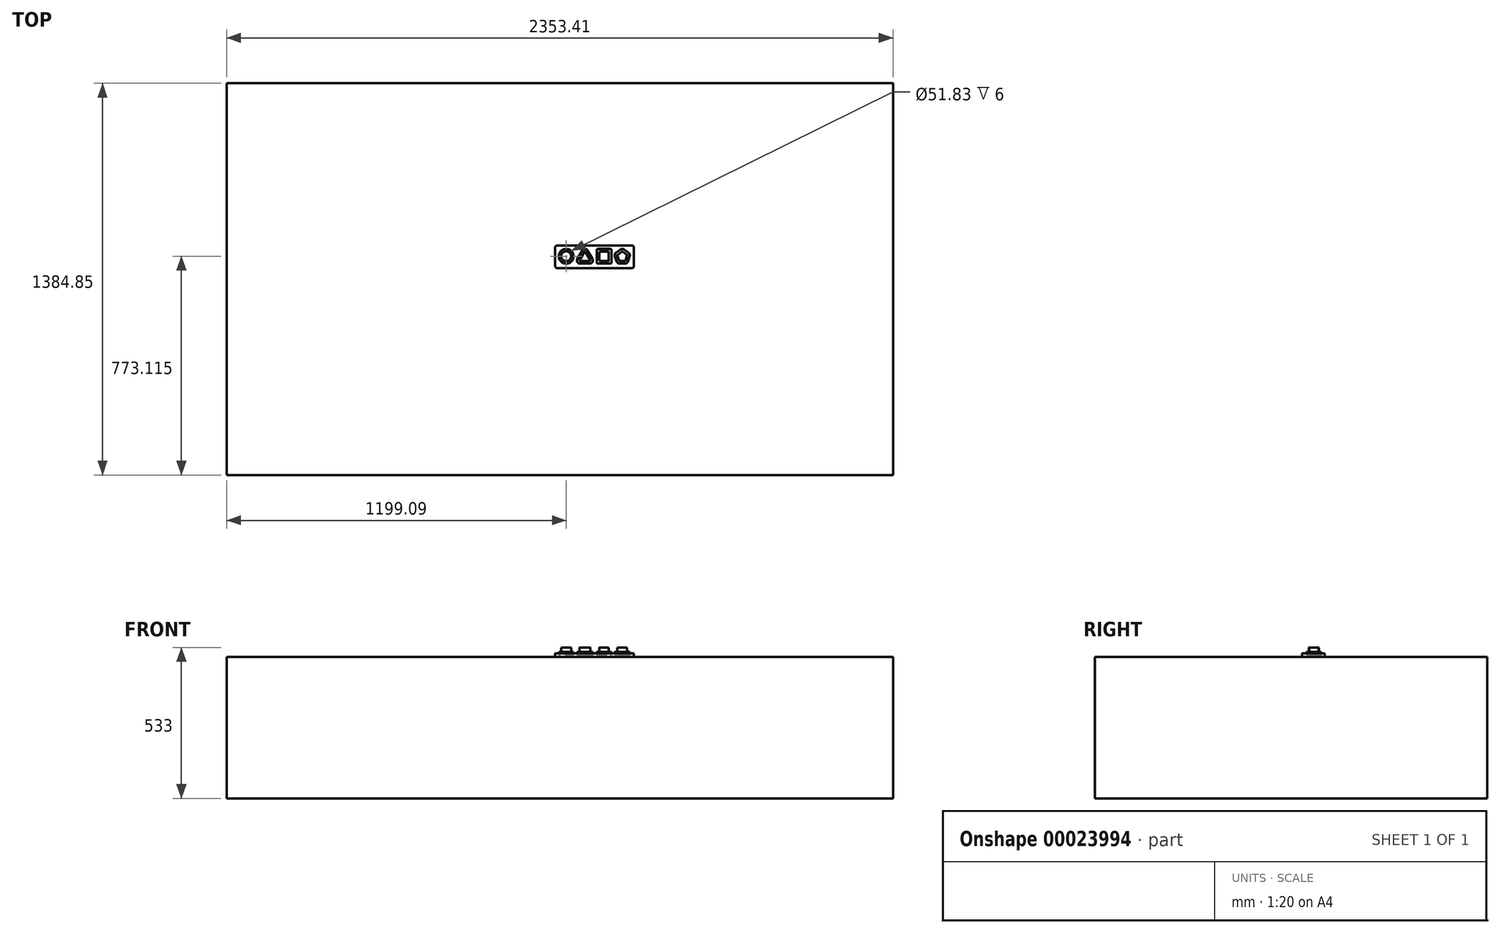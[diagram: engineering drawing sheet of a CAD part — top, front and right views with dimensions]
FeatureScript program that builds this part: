
annotation { "Feature Type Name" : "Feature", "Feature Type Description" : "" }
export const myFeature = defineFeature(function(context is Context, id is Id, definition is map)
    precondition{}
    {
        {
            var Q0;
            Q0=qCreatedBy(makeId("Top.planeOp"),FACE);
            var sketch = newSketch(context, id + "F0", { "sketchPlane" : qUnion([Q0])});
            skLineSegment(sketch, "E0.bottom", {"start": v(-140, 12) * mm, "end": v(124, 12) * mm});
            skLineSegment(sketch, "E0.top", {"start": v(-140, -68) * mm, "end": v(124, -68) * mm});
            skLineSegment(sketch, "E0.left", {"start": v(-147, 5) * mm, "end": v(-147, -61) * mm});
            skLineSegment(sketch, "E0.right", {"start": v(131, 5) * mm, "end": v(131, -61) * mm});
            skLineSegment(sketch, "E1.bottom", {"start": v(5, 0) * mm, "end": v(47, 0) * mm});
            skLineSegment(sketch, "E1.top", {"start": v(5, -52) * mm, "end": v(47, -52) * mm});
            skLineSegment(sketch, "E1.left", {"start": v(0, -5) * mm, "end": v(0, -47) * mm});
            skLineSegment(sketch, "E1.right", {"start": v(52, -5) * mm, "end": v(52, -47) * mm});
            skCircle(sketch, "E2", {"center": v(-108.08, -26.08) * mm, "radius": 25.92 * mm});
            skLineSegment(sketch, "E3", {"start": v(0, 120.87) * mm, "end": v(0, -115.92) * mm, "construction": true});
            skPoint(sketch, "E4.visualSharp", {"position": v(0, -52) * mm});
            skArc(sketch, "E4.filletArc", {"start": v(0, -47) * mm, "mid": v(1.46, -50.54) * mm, "end": v(5, -52) * mm});
            skPoint(sketch, "E5.visualSharp", {"position": v(0, 0) * mm});
            skArc(sketch, "E5.filletArc", {"start": v(5, 0) * mm, "mid": v(1.46, -1.46) * mm, "end": v(0, -5) * mm});
            skPoint(sketch, "E6.visualSharp", {"position": v(52, 0) * mm});
            skArc(sketch, "E6.filletArc", {"start": v(52, -5) * mm, "mid": v(50.54, -1.46) * mm, "end": v(47, 0) * mm});
            skPoint(sketch, "E7.visualSharp", {"position": v(52, -52) * mm});
            skArc(sketch, "E7.filletArc", {"start": v(47, -52) * mm, "mid": v(50.54, -50.54) * mm, "end": v(52, -47) * mm});
            skPoint(sketch, "E8.visualSharp", {"position": v(-1.47, -51.53) * mm});
            skPoint(sketch, "E9.visualSharp", {"position": v(-147, 12) * mm});
            skArc(sketch, "E9.filletArc", {"start": v(-140, 12) * mm, "mid": v(-144.95, 9.95) * mm, "end": v(-147, 5) * mm});
            skPoint(sketch, "E10.visualSharp", {"position": v(131, 12) * mm});
            skArc(sketch, "E10.filletArc", {"start": v(131, 5) * mm, "mid": v(128.95, 9.95) * mm, "end": v(124, 12) * mm});
            skPoint(sketch, "E11.visualSharp", {"position": v(131, -68) * mm});
            skArc(sketch, "E11.filletArc", {"start": v(124, -68) * mm, "mid": v(128.95, -65.95) * mm, "end": v(131, -61) * mm});
            skPoint(sketch, "E12.visualSharp", {"position": v(-147, -68) * mm});
            skArc(sketch, "E12.filletArc", {"start": v(-147, -61) * mm, "mid": v(-144.95, -65.95) * mm, "end": v(-140, -68) * mm});
            skLineSegment(sketch, "E13", {"start": v(-178.87, 0) * mm, "end": v(142.51, 0) * mm, "construction": true});
            skLineSegment(sketch, "E14", {"start": v(-177.03, -52) * mm, "end": v(135.64, -52) * mm, "construction": true});
            skCircle(sketch, "E15.cCircle", {"center": v(-42, -30.98) * mm, "radius": 42.04 * mm, "construction": true});
            skLineSegment(sketch, "E15.0", {"start": v(-32.47, -5.45) * mm, "end": v(-15.12, -35.5) * mm});
            skLineSegment(sketch, "E15.1", {"start": v(-24.65, -52) * mm, "end": v(-59.35, -52) * mm});
            skLineSegment(sketch, "E15.2", {"start": v(-68.88, -35.5) * mm, "end": v(-51.53, -5.45) * mm});
            skCircle(sketch, "E16.cCircle", {"center": v(90, -27.6) * mm, "radius": 30.15 * mm, "construction": true});
            skLineSegment(sketch, "E16.0", {"start": v(96.47, -2.16) * mm, "end": v(112.2, -13.6) * mm});
            skLineSegment(sketch, "E16.1", {"start": v(116.2, -25.9) * mm, "end": v(110.2, -44.4) * mm});
            skLineSegment(sketch, "E16.2", {"start": v(99.73, -52) * mm, "end": v(80.27, -52) * mm});
            skLineSegment(sketch, "E16.3", {"start": v(69.8, -44.4) * mm, "end": v(63.8, -25.9) * mm});
            skLineSegment(sketch, "E16.4", {"start": v(67.8, -13.6) * mm, "end": v(83.53, -2.16) * mm});
            skPoint(sketch, "E17.visualSharp", {"position": v(-78.4, -52) * mm});
            skArc(sketch, "E17.filletArc", {"start": v(-68.88, -35.5) * mm, "mid": v(-68.88, -46.5) * mm, "end": v(-59.35, -52) * mm});
            skPoint(sketch, "E18.visualSharp", {"position": v(-42, 11.05) * mm});
            skArc(sketch, "E18.filletArc", {"start": v(-32.47, -5.45) * mm, "mid": v(-42, 0.05) * mm, "end": v(-51.53, -5.45) * mm});
            skPoint(sketch, "E19.visualSharp", {"position": v(-5.6, -52) * mm});
            skArc(sketch, "E19.filletArc", {"start": v(-24.65, -52) * mm, "mid": v(-15.12, -46.5) * mm, "end": v(-15.12, -35.5) * mm});
            skPoint(sketch, "E20.visualSharp", {"position": v(61.33, -18.3) * mm});
            skArc(sketch, "E20.filletArc", {"start": v(67.8, -13.6) * mm, "mid": v(63.8, -19.1) * mm, "end": v(63.8, -25.9) * mm});
            skPoint(sketch, "E21.visualSharp", {"position": v(90, 2.54) * mm});
            skArc(sketch, "E21.filletArc", {"start": v(96.47, -2.16) * mm, "mid": v(90, -0.06) * mm, "end": v(83.53, -2.16) * mm});
            skPoint(sketch, "E22.visualSharp", {"position": v(118.67, -18.3) * mm});
            skArc(sketch, "E22.filletArc", {"start": v(116.2, -25.9) * mm, "mid": v(116.2, -19.1) * mm, "end": v(112.2, -13.6) * mm});
            skPoint(sketch, "E23.visualSharp", {"position": v(107.72, -52) * mm});
            skArc(sketch, "E23.filletArc", {"start": v(99.73, -52) * mm, "mid": v(106.2, -49.9) * mm, "end": v(110.2, -44.4) * mm});
            skPoint(sketch, "E24.visualSharp", {"position": v(72.28, -52) * mm});
            skArc(sketch, "E24.filletArc", {"start": v(69.8, -44.4) * mm, "mid": v(73.8, -49.9) * mm, "end": v(80.27, -52) * mm});
            skSolve(sketch);
        }
        {
            var Q0;
            Q0 = qSketchRegion(id + "F0", true);
            extrude(context, id + "F1", {"entities" : qUnion([Q0]), "depth" : 6 * mm});
        }
        {
            var Q0;
            Q0=makeQuery(id+"F1.opExtrude","CAP_FACE",FACE,{"disambiguationData":[OSD([sQuery(id+"F0.wireOp",EDGE,"E0.bottom"),sQuery(id+"F0.wireOp",EDGE,"E0.top"),sQuery(id+"F0.wireOp",EDGE,"E0.left"),sQuery(id+"F0.wireOp",EDGE,"E0.right"),sQuery(id+"F0.wireOp",EDGE,"E1.bottom"),sQuery(id+"F0.wireOp",EDGE,"E1.top"),sQuery(id+"F0.wireOp",EDGE,"E1.left"),sQuery(id+"F0.wireOp",EDGE,"E1.right"),sQuery(id+"F0.wireOp",EDGE,"E2"),sQuery(id+"F0.wireOp",EDGE,"869f132f-bd3b-4005-ba41-de87afd1fafc.0"),sQuery(id+"F0.wireOp",EDGE,"869f132f-bd3b-4005-ba41-de87afd1fafc.1"),sQuery(id+"F0.wireOp",EDGE,"869f132f-bd3b-4005-ba41-de87afd1fafc.2"),sQuery(id+"F0.wireOp",EDGE,"28d936d4-a283-45c8-93be-50b37cede906.0"),sQuery(id+"F0.wireOp",EDGE,"28d936d4-a283-45c8-93be-50b37cede906.1"),sQuery(id+"F0.wireOp",EDGE,"28d936d4-a283-45c8-93be-50b37cede906.2"),sQuery(id+"F0.wireOp",EDGE,"28d936d4-a283-45c8-93be-50b37cede906.3"),sQuery(id+"F0.wireOp",EDGE,"28d936d4-a283-45c8-93be-50b37cede906.4"),sQuery(id+"F0.wireOp",EDGE,"E4.filletArc"),sQuery(id+"F0.wireOp",EDGE,"E5.filletArc"),sQuery(id+"F0.wireOp",EDGE,"E6.filletArc"),sQuery(id+"F0.wireOp",EDGE,"E7.filletArc"),sQuery(id+"F0.wireOp",EDGE,"e9b6b36f-3266-419f-b830-8cc76e1a5d8f.filletArc"),sQuery(id+"F0.wireOp",EDGE,"cbe3ce96-ce12-412b-8ec9-2c38098c0a51.filletArc"),sQuery(id+"F0.wireOp",EDGE,"E8.filletArc"),sQuery(id+"F0.wireOp",EDGE,"ebdce603-2f92-4f1c-9763-50f2206a4805.filletArc"),sQuery(id+"F0.wireOp",EDGE,"32bf3db0-3fe5-4774-a2ea-bb73315c0dd0.filletArc"),sQuery(id+"F0.wireOp",EDGE,"89093162-53c0-41e8-8220-2e7c1048e818.filletArc"),sQuery(id+"F0.wireOp",EDGE,"d950af28-5088-4348-9f62-8025f05ed35f.filletArc"),sQuery(id+"F0.wireOp",EDGE,"a5eb8416-0ce1-40eb-8187-346b929c9b26.filletArc"),sQuery(id+"F0.wireOp",EDGE,"E9.filletArc"),sQuery(id+"F0.wireOp",EDGE,"E10.filletArc"),sQuery(id+"F0.wireOp",EDGE,"E11.filletArc"),sQuery(id+"F0.wireOp",EDGE,"E12.filletArc")])],"isStart":false});
            var sketch = newSketch(context, id + "F2", { "sketchPlane" : qUnion([Q0])});
            skCircle(sketch, "E25.0", {"center": v(-108.08, -26.08) * mm, "radius": 25.42 * mm});
            skSolve(sketch);
        }
        {
            var Q0;
            Q0 = qSketchRegion(id + "F2", true);
            extrude(context, id + "F3", {"entities" : qUnion([Q0]), "depth" : 6 * mm});
        }
        {
            var Q0;
            Q0=makeQuery(id+"F3.opExtrude","CAP_FACE",FACE,{"disambiguationData":[OSD([sQuery(id+"F2.wireOp",EDGE,"E25.0")])],"isStart":false});
            var sketch = newSketch(context, id + "F4", { "sketchPlane" : qUnion([Q0])});
            skCircle(sketch, "E26.0", {"center": v(-108.08, -26.08) * mm, "radius": 17.42 * mm});
            skSolve(sketch);
        }
        {
            var Q0;
            Q0 = qSketchRegion(id + "F4", true);
            extrude(context, id + "F5", {"entities" : qUnion([Q0]), "operationType" : NewBodyOperationType.ADD, "depth" : 15 * mm});
        }
        {
            var Q0;
            Q0=makeQuery(id+"F1.opExtrude","CAP_FACE",FACE,{"disambiguationData":[OSD([sQuery(id+"F0.wireOp",EDGE,"E0.bottom"),sQuery(id+"F0.wireOp",EDGE,"E0.top"),sQuery(id+"F0.wireOp",EDGE,"E0.left"),sQuery(id+"F0.wireOp",EDGE,"E0.right"),sQuery(id+"F0.wireOp",EDGE,"E1.bottom"),sQuery(id+"F0.wireOp",EDGE,"E1.top"),sQuery(id+"F0.wireOp",EDGE,"E1.left"),sQuery(id+"F0.wireOp",EDGE,"E1.right"),sQuery(id+"F0.wireOp",EDGE,"E2"),sQuery(id+"F0.wireOp",EDGE,"E4.filletArc"),sQuery(id+"F0.wireOp",EDGE,"E5.filletArc"),sQuery(id+"F0.wireOp",EDGE,"E6.filletArc"),sQuery(id+"F0.wireOp",EDGE,"E7.filletArc"),sQuery(id+"F0.wireOp",EDGE,"E9.filletArc"),sQuery(id+"F0.wireOp",EDGE,"E10.filletArc"),sQuery(id+"F0.wireOp",EDGE,"E11.filletArc"),sQuery(id+"F0.wireOp",EDGE,"E12.filletArc"),sQuery(id+"F0.wireOp",EDGE,"E15.0"),sQuery(id+"F0.wireOp",EDGE,"E15.1"),sQuery(id+"F0.wireOp",EDGE,"E15.2"),sQuery(id+"F0.wireOp",EDGE,"E16.0"),sQuery(id+"F0.wireOp",EDGE,"E16.1"),sQuery(id+"F0.wireOp",EDGE,"E16.2"),sQuery(id+"F0.wireOp",EDGE,"E16.3"),sQuery(id+"F0.wireOp",EDGE,"E16.4"),sQuery(id+"F0.wireOp",EDGE,"E17.filletArc"),sQuery(id+"F0.wireOp",EDGE,"E18.filletArc"),sQuery(id+"F0.wireOp",EDGE,"E19.filletArc"),sQuery(id+"F0.wireOp",EDGE,"E20.filletArc"),sQuery(id+"F0.wireOp",EDGE,"E21.filletArc"),sQuery(id+"F0.wireOp",EDGE,"E22.filletArc"),sQuery(id+"F0.wireOp",EDGE,"E23.filletArc"),sQuery(id+"F0.wireOp",EDGE,"E24.filletArc")])],"isStart":false});
            var sketch = newSketch(context, id + "F6", { "sketchPlane" : qUnion([Q0])});
            skLineSegment(sketch, "E27.0", {"start": v(-68.45, -35.75) * mm, "end": v(-51.1, -5.7) * mm});
            skArc(sketch, "E27.1", {"start": v(-68.45, -35.75) * mm, "mid": v(-68.45, -46.25) * mm, "end": v(-59.35, -51.5) * mm});
            skLineSegment(sketch, "E27.2", {"start": v(-24.65, -51.5) * mm, "end": v(-59.35, -51.5) * mm});
            skArc(sketch, "E27.3", {"start": v(-24.65, -51.5) * mm, "mid": v(-15.55, -46.25) * mm, "end": v(-15.55, -35.75) * mm});
            skLineSegment(sketch, "E27.4", {"start": v(-32.9, -5.7) * mm, "end": v(-15.55, -35.75) * mm});
            skArc(sketch, "E27.5", {"start": v(-32.9, -5.7) * mm, "mid": v(-42, -0.45) * mm, "end": v(-51.1, -5.7) * mm});
            skSolve(sketch);
        }
        {
            var Q0;
            Q0 = qSketchRegion(id + "F6", true);
            extrude(context, id + "F7", {"entities" : qUnion([Q0]), "depth" : 6 * mm});
        }
        {
            var Q0;
            Q0=makeQuery(id+"F7.opExtrude","CAP_FACE",FACE,{"disambiguationData":[OSD([sQuery(id+"F6.wireOp",EDGE,"E27.0"),sQuery(id+"F6.wireOp",EDGE,"E27.1"),sQuery(id+"F6.wireOp",EDGE,"E27.2"),sQuery(id+"F6.wireOp",EDGE,"E27.3"),sQuery(id+"F6.wireOp",EDGE,"E27.4"),sQuery(id+"F6.wireOp",EDGE,"E27.5")])],"isStart":false});
            var sketch = newSketch(context, id + "F8", { "sketchPlane" : qUnion([Q0])});
            skLineSegment(sketch, "E28.0", {"start": v(-60.65, -40.25) * mm, "end": v(-43.3, -10.2) * mm});
            skArc(sketch, "E28.1", {"start": v(-60.65, -40.25) * mm, "mid": v(-60.65, -41.75) * mm, "end": v(-59.35, -42.5) * mm});
            skLineSegment(sketch, "E28.2", {"start": v(-24.65, -42.5) * mm, "end": v(-59.35, -42.5) * mm});
            skArc(sketch, "E28.3", {"start": v(-24.65, -42.5) * mm, "mid": v(-23.35, -41.75) * mm, "end": v(-23.35, -40.25) * mm});
            skLineSegment(sketch, "E28.4", {"start": v(-40.7, -10.2) * mm, "end": v(-23.35, -40.25) * mm});
            skArc(sketch, "E28.5", {"start": v(-40.7, -10.2) * mm, "mid": v(-42, -9.45) * mm, "end": v(-43.3, -10.2) * mm});
            skSolve(sketch);
        }
        {
            var Q0;
            Q0 = qSketchRegion(id + "F8", true);
            extrude(context, id + "F9", {"entities" : qUnion([Q0]), "operationType" : NewBodyOperationType.ADD, "depth" : 15 * mm});
        }
        {
            var Q0;
            Q0=makeQuery(id+"F1.opExtrude","CAP_FACE",FACE,{"disambiguationData":[OSD([sQuery(id+"F0.wireOp",EDGE,"E0.bottom"),sQuery(id+"F0.wireOp",EDGE,"E0.top"),sQuery(id+"F0.wireOp",EDGE,"E0.left"),sQuery(id+"F0.wireOp",EDGE,"E0.right"),sQuery(id+"F0.wireOp",EDGE,"E1.bottom"),sQuery(id+"F0.wireOp",EDGE,"E1.top"),sQuery(id+"F0.wireOp",EDGE,"E1.left"),sQuery(id+"F0.wireOp",EDGE,"E1.right"),sQuery(id+"F0.wireOp",EDGE,"E2"),sQuery(id+"F0.wireOp",EDGE,"E4.filletArc"),sQuery(id+"F0.wireOp",EDGE,"E5.filletArc"),sQuery(id+"F0.wireOp",EDGE,"E6.filletArc"),sQuery(id+"F0.wireOp",EDGE,"E7.filletArc"),sQuery(id+"F0.wireOp",EDGE,"E9.filletArc"),sQuery(id+"F0.wireOp",EDGE,"E10.filletArc"),sQuery(id+"F0.wireOp",EDGE,"E11.filletArc"),sQuery(id+"F0.wireOp",EDGE,"E12.filletArc"),sQuery(id+"F0.wireOp",EDGE,"E15.0"),sQuery(id+"F0.wireOp",EDGE,"E15.1"),sQuery(id+"F0.wireOp",EDGE,"E15.2"),sQuery(id+"F0.wireOp",EDGE,"E16.0"),sQuery(id+"F0.wireOp",EDGE,"E16.1"),sQuery(id+"F0.wireOp",EDGE,"E16.2"),sQuery(id+"F0.wireOp",EDGE,"E16.3"),sQuery(id+"F0.wireOp",EDGE,"E16.4"),sQuery(id+"F0.wireOp",EDGE,"E17.filletArc"),sQuery(id+"F0.wireOp",EDGE,"E18.filletArc"),sQuery(id+"F0.wireOp",EDGE,"E19.filletArc"),sQuery(id+"F0.wireOp",EDGE,"E20.filletArc"),sQuery(id+"F0.wireOp",EDGE,"E21.filletArc"),sQuery(id+"F0.wireOp",EDGE,"E22.filletArc"),sQuery(id+"F0.wireOp",EDGE,"E23.filletArc"),sQuery(id+"F0.wireOp",EDGE,"E24.filletArc")])],"isStart":false});
            var sketch = newSketch(context, id + "F10", { "sketchPlane" : qUnion([Q0])});
            skArc(sketch, "E29.0", {"start": v(5, -0.5) * mm, "mid": v(1.82, -1.82) * mm, "end": v(0.5, -5) * mm});
            skLineSegment(sketch, "E29.1", {"start": v(0.5, -5) * mm, "end": v(0.5, -47) * mm});
            skArc(sketch, "E29.2", {"start": v(0.5, -47) * mm, "mid": v(1.82, -50.18) * mm, "end": v(5, -51.5) * mm});
            skLineSegment(sketch, "E29.3", {"start": v(5, -51.5) * mm, "end": v(47, -51.5) * mm});
            skArc(sketch, "E29.4", {"start": v(47, -51.5) * mm, "mid": v(50.18, -50.18) * mm, "end": v(51.5, -47) * mm});
            skLineSegment(sketch, "E29.5", {"start": v(5, -0.5) * mm, "end": v(47, -0.5) * mm});
            skLineSegment(sketch, "E29.6", {"start": v(51.5, -5) * mm, "end": v(51.5, -47) * mm});
            skArc(sketch, "E29.7", {"start": v(51.5, -5) * mm, "mid": v(50.18, -1.82) * mm, "end": v(47, -0.5) * mm});
            skSolve(sketch);
        }
        {
            var Q0;
            Q0 = qSketchRegion(id + "F10", true);
            extrude(context, id + "F11", {"entities" : qUnion([Q0]), "depth" : 6 * mm});
        }
        {
            var Q0;
            Q0=makeQuery(id+"F11.opExtrude","CAP_FACE",FACE,{"disambiguationData":[OSD([sQuery(id+"F10.wireOp",EDGE,"E29.0"),sQuery(id+"F10.wireOp",EDGE,"E29.1"),sQuery(id+"F10.wireOp",EDGE,"E29.2"),sQuery(id+"F10.wireOp",EDGE,"E29.3"),sQuery(id+"F10.wireOp",EDGE,"E29.4"),sQuery(id+"F10.wireOp",EDGE,"E29.5"),sQuery(id+"F10.wireOp",EDGE,"E29.6"),sQuery(id+"F10.wireOp",EDGE,"E29.7")])],"isStart":false});
            var sketch = newSketch(context, id + "F12", { "sketchPlane" : qUnion([Q0])});
            skLineSegment(sketch, "E30.0", {"start": v(11.5, -9.5) * mm, "end": v(40.5, -9.5) * mm});
            skLineSegment(sketch, "E30.1", {"start": v(9.5, -11.5) * mm, "end": v(9.5, -40.5) * mm});
            skLineSegment(sketch, "E30.2", {"start": v(11.5, -42.5) * mm, "end": v(40.5, -42.5) * mm});
            skLineSegment(sketch, "E30.3", {"start": v(42.5, -11.5) * mm, "end": v(42.5, -40.5) * mm});
            skPoint(sketch, "E31.visualSharp", {"position": v(9.5, -9.5) * mm});
            skArc(sketch, "E31.filletArc", {"start": v(11.5, -9.5) * mm, "mid": v(10.09, -10.09) * mm, "end": v(9.5, -11.5) * mm});
            skPoint(sketch, "E32.visualSharp", {"position": v(42.5, -9.5) * mm});
            skArc(sketch, "E32.filletArc", {"start": v(42.5, -11.5) * mm, "mid": v(41.91, -10.09) * mm, "end": v(40.5, -9.5) * mm});
            skPoint(sketch, "E33.visualSharp", {"position": v(42.5, -42.5) * mm});
            skArc(sketch, "E33.filletArc", {"start": v(40.5, -42.5) * mm, "mid": v(41.91, -41.91) * mm, "end": v(42.5, -40.5) * mm});
            skPoint(sketch, "E34.visualSharp", {"position": v(9.5, -42.5) * mm});
            skArc(sketch, "E34.filletArc", {"start": v(9.5, -40.5) * mm, "mid": v(10.09, -41.91) * mm, "end": v(11.5, -42.5) * mm});
            skSolve(sketch);
        }
        {
            var Q0;
            Q0 = qSketchRegion(id + "F12", true);
            extrude(context, id + "F13", {"entities" : qUnion([Q0]), "operationType" : NewBodyOperationType.ADD, "depth" : 15 * mm});
        }
        {
            var Q0;
            Q0=makeQuery(id+"F1.opExtrude","CAP_FACE",FACE,{"disambiguationData":[OSD([sQuery(id+"F0.wireOp",EDGE,"E0.bottom"),sQuery(id+"F0.wireOp",EDGE,"E0.top"),sQuery(id+"F0.wireOp",EDGE,"E0.left"),sQuery(id+"F0.wireOp",EDGE,"E0.right"),sQuery(id+"F0.wireOp",EDGE,"E1.bottom"),sQuery(id+"F0.wireOp",EDGE,"E1.top"),sQuery(id+"F0.wireOp",EDGE,"E1.left"),sQuery(id+"F0.wireOp",EDGE,"E1.right"),sQuery(id+"F0.wireOp",EDGE,"E2"),sQuery(id+"F0.wireOp",EDGE,"E4.filletArc"),sQuery(id+"F0.wireOp",EDGE,"E5.filletArc"),sQuery(id+"F0.wireOp",EDGE,"E6.filletArc"),sQuery(id+"F0.wireOp",EDGE,"E7.filletArc"),sQuery(id+"F0.wireOp",EDGE,"E9.filletArc"),sQuery(id+"F0.wireOp",EDGE,"E10.filletArc"),sQuery(id+"F0.wireOp",EDGE,"E11.filletArc"),sQuery(id+"F0.wireOp",EDGE,"E12.filletArc"),sQuery(id+"F0.wireOp",EDGE,"E15.0"),sQuery(id+"F0.wireOp",EDGE,"E15.1"),sQuery(id+"F0.wireOp",EDGE,"E15.2"),sQuery(id+"F0.wireOp",EDGE,"E16.0"),sQuery(id+"F0.wireOp",EDGE,"E16.1"),sQuery(id+"F0.wireOp",EDGE,"E16.2"),sQuery(id+"F0.wireOp",EDGE,"E16.3"),sQuery(id+"F0.wireOp",EDGE,"E16.4"),sQuery(id+"F0.wireOp",EDGE,"E17.filletArc"),sQuery(id+"F0.wireOp",EDGE,"E18.filletArc"),sQuery(id+"F0.wireOp",EDGE,"E19.filletArc"),sQuery(id+"F0.wireOp",EDGE,"E20.filletArc"),sQuery(id+"F0.wireOp",EDGE,"E21.filletArc"),sQuery(id+"F0.wireOp",EDGE,"E22.filletArc"),sQuery(id+"F0.wireOp",EDGE,"E23.filletArc"),sQuery(id+"F0.wireOp",EDGE,"E24.filletArc")])],"isStart":false});
            var sketch = newSketch(context, id + "F14", { "sketchPlane" : qUnion([Q0])});
            skArc(sketch, "E35.0", {"start": v(68.09, -14) * mm, "mid": v(64.27, -19.25) * mm, "end": v(64.27, -25.74) * mm});
            skLineSegment(sketch, "E35.1", {"start": v(70.29, -44.24) * mm, "end": v(64.27, -25.74) * mm});
            skArc(sketch, "E35.2", {"start": v(70.29, -44.24) * mm, "mid": v(74.1, -49.5) * mm, "end": v(80.27, -51.5) * mm});
            skLineSegment(sketch, "E35.3", {"start": v(99.73, -51.5) * mm, "end": v(80.27, -51.5) * mm});
            skArc(sketch, "E35.4", {"start": v(99.73, -51.5) * mm, "mid": v(105.9, -49.5) * mm, "end": v(109.71, -44.24) * mm});
            skLineSegment(sketch, "E35.5", {"start": v(68.09, -14) * mm, "end": v(83.83, -2.56) * mm});
            skLineSegment(sketch, "E35.6", {"start": v(115.73, -25.74) * mm, "end": v(109.71, -44.24) * mm});
            skArc(sketch, "E35.7", {"start": v(115.73, -25.74) * mm, "mid": v(115.73, -19.25) * mm, "end": v(111.91, -14) * mm});
            skLineSegment(sketch, "E35.8", {"start": v(96.17, -2.56) * mm, "end": v(111.91, -14) * mm});
            skArc(sketch, "E35.9", {"start": v(96.17, -2.56) * mm, "mid": v(90, -0.56) * mm, "end": v(83.83, -2.56) * mm});
            skSolve(sketch);
        }
        {
            var Q0;
            Q0 = qSketchRegion(id + "F14", true);
            extrude(context, id + "F15", {"entities" : qUnion([Q0]), "depth" : 6 * mm});
        }
        {
            var Q0;
            Q0=makeQuery(id+"F15.opExtrude","CAP_FACE",FACE,{"disambiguationData":[OSD([sQuery(id+"F14.wireOp",EDGE,"E35.0"),sQuery(id+"F14.wireOp",EDGE,"E35.1"),sQuery(id+"F14.wireOp",EDGE,"E35.2"),sQuery(id+"F14.wireOp",EDGE,"E35.3"),sQuery(id+"F14.wireOp",EDGE,"E35.4"),sQuery(id+"F14.wireOp",EDGE,"E35.5"),sQuery(id+"F14.wireOp",EDGE,"E35.6"),sQuery(id+"F14.wireOp",EDGE,"E35.7"),sQuery(id+"F14.wireOp",EDGE,"E35.8"),sQuery(id+"F14.wireOp",EDGE,"E35.9")])],"isStart":false});
            var sketch = newSketch(context, id + "F16", { "sketchPlane" : qUnion([Q0])});
            skArc(sketch, "E36.0", {"start": v(90.88, -9.84) * mm, "mid": v(90, -9.56) * mm, "end": v(89.12, -9.84) * mm});
            skLineSegment(sketch, "E36.1", {"start": v(73.38, -21.28) * mm, "end": v(89.12, -9.84) * mm});
            skArc(sketch, "E36.2", {"start": v(73.38, -21.28) * mm, "mid": v(72.83, -22.03) * mm, "end": v(72.83, -22.96) * mm});
            skLineSegment(sketch, "E36.3", {"start": v(78.84, -41.46) * mm, "end": v(72.83, -22.96) * mm});
            skArc(sketch, "E36.4", {"start": v(78.84, -41.46) * mm, "mid": v(79.39, -42.21) * mm, "end": v(80.27, -42.5) * mm});
            skLineSegment(sketch, "E36.5", {"start": v(90.88, -9.84) * mm, "end": v(106.62, -21.28) * mm});
            skLineSegment(sketch, "E36.6", {"start": v(99.73, -42.5) * mm, "end": v(80.27, -42.5) * mm});
            skArc(sketch, "E36.7", {"start": v(99.73, -42.5) * mm, "mid": v(100.61, -42.21) * mm, "end": v(101.16, -41.46) * mm});
            skLineSegment(sketch, "E36.8", {"start": v(107.17, -22.96) * mm, "end": v(101.16, -41.46) * mm});
            skArc(sketch, "E36.9", {"start": v(107.17, -22.96) * mm, "mid": v(107.17, -22.03) * mm, "end": v(106.62, -21.28) * mm});
            skSolve(sketch);
        }
        {
            var Q0;
            Q0 = qSketchRegion(id + "F16", true);
            extrude(context, id + "F17", {"entities" : qUnion([Q0]), "operationType" : NewBodyOperationType.ADD, "depth" : 15 * mm});
        }
        {
            var Q0;
            Q0=makeQuery(id+"F1.opExtrude","CAP_FACE",FACE,{"disambiguationData":[OSD([sQuery(id+"F0.wireOp",EDGE,"E0.bottom"),sQuery(id+"F0.wireOp",EDGE,"E0.top"),sQuery(id+"F0.wireOp",EDGE,"E0.left"),sQuery(id+"F0.wireOp",EDGE,"E0.right"),sQuery(id+"F0.wireOp",EDGE,"E1.bottom"),sQuery(id+"F0.wireOp",EDGE,"E1.top"),sQuery(id+"F0.wireOp",EDGE,"E1.left"),sQuery(id+"F0.wireOp",EDGE,"E1.right"),sQuery(id+"F0.wireOp",EDGE,"E2"),sQuery(id+"F0.wireOp",EDGE,"E4.filletArc"),sQuery(id+"F0.wireOp",EDGE,"E5.filletArc"),sQuery(id+"F0.wireOp",EDGE,"E6.filletArc"),sQuery(id+"F0.wireOp",EDGE,"E7.filletArc"),sQuery(id+"F0.wireOp",EDGE,"E9.filletArc"),sQuery(id+"F0.wireOp",EDGE,"E10.filletArc"),sQuery(id+"F0.wireOp",EDGE,"E11.filletArc"),sQuery(id+"F0.wireOp",EDGE,"E12.filletArc"),sQuery(id+"F0.wireOp",EDGE,"E15.0"),sQuery(id+"F0.wireOp",EDGE,"E15.1"),sQuery(id+"F0.wireOp",EDGE,"E15.2"),sQuery(id+"F0.wireOp",EDGE,"E16.0"),sQuery(id+"F0.wireOp",EDGE,"E16.1"),sQuery(id+"F0.wireOp",EDGE,"E16.2"),sQuery(id+"F0.wireOp",EDGE,"E16.3"),sQuery(id+"F0.wireOp",EDGE,"E16.4"),sQuery(id+"F0.wireOp",EDGE,"E17.filletArc"),sQuery(id+"F0.wireOp",EDGE,"E18.filletArc"),sQuery(id+"F0.wireOp",EDGE,"E19.filletArc"),sQuery(id+"F0.wireOp",EDGE,"E20.filletArc"),sQuery(id+"F0.wireOp",EDGE,"E21.filletArc"),sQuery(id+"F0.wireOp",EDGE,"E22.filletArc"),sQuery(id+"F0.wireOp",EDGE,"E23.filletArc"),sQuery(id+"F0.wireOp",EDGE,"E24.filletArc")])],"isStart":true});
            var sketch = newSketch(context, id + "F18", { "sketchPlane" : qUnion([Q0])});
            skArc(sketch, "E37.0", {"start": v(-140, -12) * mm, "mid": v(-144.95, -9.95) * mm, "end": v(-147, -5) * mm});
            skLineSegment(sketch, "E37.1", {"start": v(-147, -5) * mm, "end": v(-147, 61) * mm});
            skArc(sketch, "E37.2", {"start": v(-147, 61) * mm, "mid": v(-144.95, 65.95) * mm, "end": v(-140, 68) * mm});
            skLineSegment(sketch, "E37.3", {"start": v(-140, 68) * mm, "end": v(124, 68) * mm});
            skArc(sketch, "E37.4", {"start": v(124, 68) * mm, "mid": v(128.95, 65.95) * mm, "end": v(131, 61) * mm});
            skLineSegment(sketch, "E37.5", {"start": v(-140, -12) * mm, "end": v(124, -12) * mm});
            skLineSegment(sketch, "E37.6", {"start": v(131, -5) * mm, "end": v(131, 61) * mm});
            skArc(sketch, "E37.7", {"start": v(131, -5) * mm, "mid": v(128.95, -9.95) * mm, "end": v(124, -12) * mm});
            skSolve(sketch);
        }
        {
            var Q0;
            Q0 = qSketchRegion(id + "F18", true);
            extrude(context, id + "F19", {"entities" : qUnion([Q0]), "operationType" : NewBodyOperationType.ADD, "depth" : 6 * mm});
        }
        {
            var Q0;
            Q0=makeQuery(id+"F19.opExtrude","CAP_FACE",FACE,{"disambiguationData":[OSD([sQuery(id+"F18.wireOp",EDGE,"E37.0"),sQuery(id+"F18.wireOp",EDGE,"E37.1"),sQuery(id+"F18.wireOp",EDGE,"E37.2"),sQuery(id+"F18.wireOp",EDGE,"E37.3"),sQuery(id+"F18.wireOp",EDGE,"E37.4"),sQuery(id+"F18.wireOp",EDGE,"E37.5"),sQuery(id+"F18.wireOp",EDGE,"E37.6"),sQuery(id+"F18.wireOp",EDGE,"E37.7")])],"isStart":false});
            var sketch = newSketch(context, id + "F20", { "sketchPlane" : qUnion([Q0])});
            skLineSegment(sketch, "E38.bottom", {"start": v(1046.24, -585.65) * mm, "end": v(-1307.17, -585.65) * mm});
            skLineSegment(sketch, "E38.top", {"start": v(1046.24, 799.2) * mm, "end": v(-1307.17, 799.2) * mm});
            skLineSegment(sketch, "E38.left", {"start": v(1046.24, -585.65) * mm, "end": v(1046.24, 799.2) * mm});
            skLineSegment(sketch, "E38.right", {"start": v(-1307.17, -585.65) * mm, "end": v(-1307.17, 799.2) * mm});
            skSolve(sketch);
        }
        {
            var Q0;
            Q0 = qSketchRegion(id + "F20", true);
            extrude(context, id + "F21", {"entities" : qUnion([Q0]), "depth" : 500 * mm});
        }
    });
